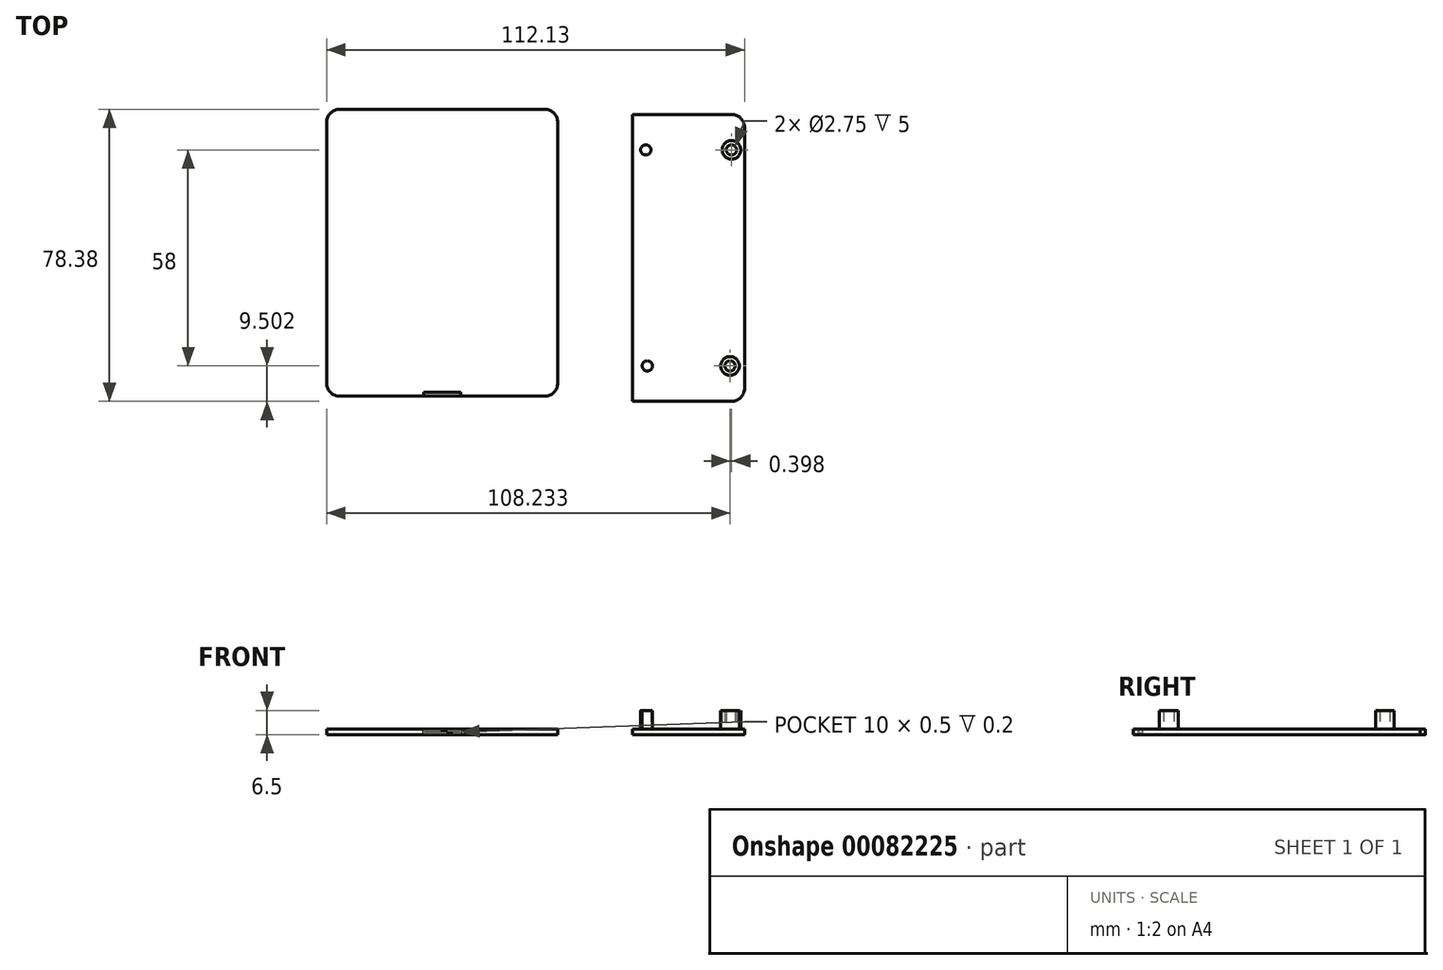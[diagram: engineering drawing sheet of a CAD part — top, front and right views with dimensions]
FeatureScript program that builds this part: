
annotation { "Feature Type Name" : "Feature", "Feature Type Description" : "" }
export const myFeature = defineFeature(function(context is Context, id is Id, definition is map)
    precondition{}
    {
        {
            var Q0;
            Q0=qCreatedBy(makeId("Top.planeOp"),FACE);
            var sketch = newSketch(context, id + "F0", { "sketchPlane" : qUnion([Q0])});
            skLineSegment(sketch, "E0.bottom", {"start": v(-72.46, 37.76) * mm, "end": v(-10.46, 37.76) * mm});
            skLineSegment(sketch, "E0.top", {"start": v(-72.46, -39.24) * mm, "end": v(-10.46, -39.24) * mm});
            skLineSegment(sketch, "E0.left", {"start": v(-72.46, 37.76) * mm, "end": v(-72.46, -39.24) * mm});
            skLineSegment(sketch, "E0.right", {"start": v(-10.46, 37.76) * mm, "end": v(-10.46, -39.24) * mm});
            skLineSegment(sketch, "E1.bottom", {"start": v(9.67, 36.38) * mm, "end": v(39.67, 36.38) * mm});
            skLineSegment(sketch, "E1.top", {"start": v(9.67, -40.62) * mm, "end": v(39.67, -40.62) * mm});
            skLineSegment(sketch, "E1.left", {"start": v(9.67, 36.38) * mm, "end": v(9.67, -40.62) * mm});
            skLineSegment(sketch, "E1.right", {"start": v(39.67, 36.38) * mm, "end": v(39.67, -40.62) * mm});
            skSolve(sketch);
        }
        {
            var Q0;
            Q0=makeQuery(id+"F0.imprint","IMPRINT",FACE,{"disambiguationData":[TD([[makeQuery(id+"F0.imprint","IMPRINT",EDGE,{"derivedFrom":sQuery(id+"F0.wireOp",EDGE,"E0.bottom")}),-1.0]])]});
            var Q1;
            Q1=makeQuery(id+"F0.imprint","IMPRINT",FACE,{"disambiguationData":[TD([[makeQuery(id+"F0.imprint","IMPRINT",EDGE,{"derivedFrom":sQuery(id+"F0.wireOp",EDGE,"E1.bottom")}),-1.0]])]});
            extrude(context, id + "F1", {"entities" : qUnion([Q0, Q1]), "depth" : 1.5 * mm});
        }
        {
            var Q0;
            Q0=makeQuery(id+"F1.opExtrude","SWEPT_EDGE",EDGE,{"disambiguationData":[OSD([sQuery(id+"F0.wireOp",EDGE,"E0.top"),sQuery(id+"F0.wireOp",EDGE,"E0.right")])]});
            var Q1;
            Q1=makeQuery(id+"F1.opExtrude","SWEPT_EDGE",EDGE,{"disambiguationData":[OSD([sQuery(id+"F0.wireOp",EDGE,"E0.top"),sQuery(id+"F0.wireOp",EDGE,"E0.left")])]});
            var Q2;
            Q2=makeQuery(id+"F1.opExtrude","SWEPT_EDGE",EDGE,{"disambiguationData":[OSD([sQuery(id+"F0.wireOp",EDGE,"E0.bottom"),sQuery(id+"F0.wireOp",EDGE,"E0.left")])]});
            var Q3;
            Q3=makeQuery(id+"F1.opExtrude","SWEPT_EDGE",EDGE,{"disambiguationData":[OSD([sQuery(id+"F0.wireOp",EDGE,"E0.bottom"),sQuery(id+"F0.wireOp",EDGE,"E0.right")])]});
            var Q4;
            Q4=makeQuery(id+"F1.opExtrude","SWEPT_EDGE",EDGE,{"disambiguationData":[OSD([sQuery(id+"F0.wireOp",EDGE,"E1.bottom"),sQuery(id+"F0.wireOp",EDGE,"E1.right")])]});
            var Q5;
            Q5=makeQuery(id+"F1.opExtrude","SWEPT_EDGE",EDGE,{"disambiguationData":[OSD([sQuery(id+"F0.wireOp",EDGE,"E1.top"),sQuery(id+"F0.wireOp",EDGE,"E1.right")])]});
            fillet(context, id + "F2", {"entities" : qUnion([Q0, Q1, Q2, Q3, Q4, Q5]), "radius" : 3.5 * mm, "tangentPropagation" : true, "allowEdgeOverflow" : false});
        }
        {
            var Q0;
            Q0=makeQuery(id+"F1.opExtrude","CAP_FACE",FACE,{"disambiguationData":[OSD([sQuery(id+"F0.wireOp",EDGE,"E1.bottom"),sQuery(id+"F0.wireOp",EDGE,"E1.top"),sQuery(id+"F0.wireOp",EDGE,"E1.left"),sQuery(id+"F0.wireOp",EDGE,"E1.right")])],"isStart":false});
            var sketch = newSketch(context, id + "F3", { "sketchPlane" : qUnion([Q0])});
            skLineSegment(sketch, "E2.bottom", {"start": v(9.67, 30.38) * mm, "end": v(39.67, 30.38) * mm});
            skLineSegment(sketch, "E2.top", {"start": v(9.67, -34.62) * mm, "end": v(39.67, -34.62) * mm});
            skLineSegment(sketch, "E2.left", {"start": v(9.67, 30.38) * mm, "end": v(9.67, -34.62) * mm});
            skLineSegment(sketch, "E2.right", {"start": v(39.67, 30.38) * mm, "end": v(39.67, -34.62) * mm});
            skCircle(sketch, "E3", {"center": v(35.77, -31.12) * mm, "radius": 1.38 * mm});
            skCircle(sketch, "E4", {"center": v(35.77, -31.12) * mm, "radius": 2.5 * mm});
            skCircle(sketch, "E5", {"center": v(36.17, 26.88) * mm, "radius": 1.38 * mm});
            skCircle(sketch, "E6", {"center": v(36.17, 26.88) * mm, "radius": 2.5 * mm});
            skLineSegment(sketch, "E7", {"start": v(39.67, -2.12) * mm, "end": v(9.67, -2.12) * mm});
            skLineSegment(sketch, "E8", {"start": v(24.67, 30.38) * mm, "end": v(24.67, -34.62) * mm});
            skCircle(sketch, "E9.MirrorC", {"center": v(13.57, -31.12) * mm, "radius": 1.38 * mm});
            skCircle(sketch, "E10.MirrorC", {"center": v(13.57, -31.12) * mm, "radius": 2.5 * mm});
            skCircle(sketch, "E11.MirrorC", {"center": v(13.17, 26.88) * mm, "radius": 1.38 * mm});
            skCircle(sketch, "E12.MirrorC", {"center": v(13.17, 26.88) * mm, "radius": 2.5 * mm});
            skSolve(sketch);
        }
        {
            var Q0;
            Q0=makeQuery(id+"F3.imprint","IMPRINT",FACE,{"disambiguationData":[TD([[makeQuery(id+"F3.imprint","IMPRINT",EDGE,{"derivedFrom":sQuery(id+"F3.wireOp",EDGE,"E9.MirrorC")}),1.0]])]});
            var Q1;
            Q1=makeQuery(id+"F3.imprint","IMPRINT",FACE,{"disambiguationData":[TD([[makeQuery(id+"F3.imprint","IMPRINT",EDGE,{"derivedFrom":sQuery(id+"F3.wireOp",EDGE,"E3")}),-1.0]])]});
            var Q2;
            Q2=makeQuery(id+"F3.imprint","IMPRINT",FACE,{"disambiguationData":[TD([[makeQuery(id+"F3.imprint","IMPRINT",EDGE,{"derivedFrom":sQuery(id+"F3.wireOp",EDGE,"E5")}),-1.0]])]});
            var Q3;
            Q3=makeQuery(id+"F3.imprint","IMPRINT",FACE,{"disambiguationData":[TD([[makeQuery(id+"F3.imprint","IMPRINT",EDGE,{"derivedFrom":sQuery(id+"F3.wireOp",EDGE,"E11.MirrorC")}),1.0]])]});
            extrude(context, id + "F4", {"entities" : qUnion([Q0, Q1, Q2, Q3]), "operationType" : NewBodyOperationType.ADD, "depth" : 5 * mm});
        }
        {
            var Q0;
            Q0=makeQuery(id+"F1.opExtrude","CAP_FACE",FACE,{"disambiguationData":[OSD([sQuery(id+"F0.wireOp",EDGE,"E0.bottom"),sQuery(id+"F0.wireOp",EDGE,"E0.top"),sQuery(id+"F0.wireOp",EDGE,"E0.left"),sQuery(id+"F0.wireOp",EDGE,"E0.right")])],"isStart":false});
            var sketch = newSketch(context, id + "F5", { "sketchPlane" : qUnion([Q0])});
            skLineSegment(sketch, "E13.top", {"start": v(-46.46, -38.24) * mm, "end": v(-36.46, -38.24) * mm});
            skLineSegment(sketch, "E13.left", {"start": v(-46.46, -39.24) * mm, "end": v(-46.46, -38.24) * mm});
            skLineSegment(sketch, "E13.right", {"start": v(-36.46, -39.24) * mm, "end": v(-36.46, -38.24) * mm});
            skLineSegment(sketch, "E14", {"start": v(-46.46, -39.24) * mm, "end": v(-36.46, -39.24) * mm});
            skSolve(sketch);
        }
        {
            var Q0;
            Q0=makeQuery(id+"F5.imprint","IMPRINT",FACE,{"disambiguationData":[TD([[makeQuery(id+"F5.imprint","IMPRINT",EDGE,{"derivedFrom":sQuery(id+"F5.wireOp",EDGE,"E13.top")}),-1.0]])]});
            extrude(context, id + "F6", {"entities" : qUnion([Q0]), "operationType" : NewBodyOperationType.REMOVE, "oppositeDirection" : true, "depth" : 1 * mm});
        }
        {
            var Q0;
            Q0=makeQuery(id+"F6.boolean.opBoolean","COPY",FACE,{"derivedFrom":makeQuery(id+"F6.opExtrude","SWEPT_FACE",FACE,{"disambiguationData":[OSD([sQuery(id+"F5.wireOp",EDGE,"E13.top")])]})});
            var sketch = newSketch(context, id + "F7", { "sketchPlane" : qUnion([Q0])});
            skLineSegment(sketch, "E15.bottom", {"start": v(-46.46, 1) * mm, "end": v(-36.46, 1) * mm});
            skLineSegment(sketch, "E15.top", {"start": v(-46.46, 0.5) * mm, "end": v(-36.46, 0.5) * mm});
            skLineSegment(sketch, "E15.left", {"start": v(-46.46, 1) * mm, "end": v(-46.46, 0.5) * mm});
            skLineSegment(sketch, "E15.right", {"start": v(-36.46, 1) * mm, "end": v(-36.46, 0.5) * mm});
            skSolve(sketch);
        }
        {
            var Q0;
            Q0=makeQuery(id+"F7.imprint","IMPRINT",FACE,{"disambiguationData":[TD([[makeQuery(id+"F7.imprint","IMPRINT",EDGE,{"derivedFrom":sQuery(id+"F7.wireOp",EDGE,"E15.bottom")}),-1.0]])]});
            extrude(context, id + "F8", {"entities" : qUnion([Q0]), "operationType" : NewBodyOperationType.REMOVE, "oppositeDirection" : true, "depth" : 0.2 * mm});
        }
    });
